# Revit family: LRTF
name_source: partatom
category: Lighting Fixtures
units: mm (PartAtom-declared; Revit-internal decimal feet)

## family parameters
Cut with Voids When Loaded = No
Host = Face
Light Source = Yes
Part Type = Normal
Room Calculation Point = No
Round Connector Dimension = Use Diameter
Shared = No

## types (8) — shared parameters
Assembly Code = D5020200
Color Filter = 16777215
Default Elevation = 4' - 0"
Description = LED Troffer Dish Low Profile Diffuser
Dimming Lamp Color Temperature Shift = <None>
Emit Shape Visible in Rendering = No
Housing Finish = Metal - Viscor - White
Lamp = LED
Lens Finish = Acrylic - Viscor - Frosted Ribbed Linear
Manufacturer = VISIONEERING by VISCOR
Model = LRTF
Tilt Angle = -90.00°
URL = https://www.viscor.com
Voltage = 120 V

## per-type parameters (varying)
| type | Apparent Load | Emit from Rectangle Length | Emit from Rectangle Width | Height of Fixture | Lamp Wattage | Length | Photometric Web File | Reflector Wdith | Width |
| LRTF1X4-LED840K050LUNV | 37 VA | 3' - 11 3/4" | 0' - 11 3/4" | 0' - 2 1/2" | 37 VA | 3' - 11 3/4" | LRTF1X4-LED840K050LUNV-G001831.IES | 0' - 5 7/8" | 0' - 11 3/4" |
| LRTF1x1-LED840K016LUNV | 17 VA | 1' - 1 15/16" | 1' - 1 15/16" | 0' - 3 3/8" | 17 VA | 1' - 1 15/16" | LRTF1x1-LED840K016LUNV.ies | 0' - 6 31/32" | 1' - 1 15/16" |
| LRTF2x2-LED840K038LUNV | 30 VA | 1' - 11 3/4" | 1' - 11 3/4" | 0' - 2 1/2" | 30 VA | 1' - 11 3/4" | LRTF2x2-LED840K038LUNV-G001332.IES | 0' - 11 7/8" | 1' - 11 3/4" |
| LRTF2X4-LED840K040LUNV | 32 VA | 3' - 11 3/4" | 1' - 11 3/4" | 0' - 2 1/2" | 32 VA | 3' - 11 3/4" | LRTF2X4-LED840K040LUNV.ies | 0' - 11 7/8" | 1' - 11 3/4" |
| LRTF30x30-LED840K038LUNV | 31 VA | 2' - 5 3/4" | 2' - 5 3/4" | 0' - 2 1/2" | 31 VA | 2' - 5 3/4" | LRTF30X30-LED840K038LUNV.ies | 1' - 2 7/8" | 2' - 5 3/4" |
| LRTF20x60-LED835K050LUNV | 37 VA | 4' - 11 3/4" | 1' - 7 3/4" | 0' - 2 1/2" | 37 VA | 4' - 11 3/4" | LRTF20X60-LED835K050LUNV.ies | 0' - 9 7/8" | 1' - 7 3/4" |
| LRTF2X4-LED840K050LUNV | 37 VA | 3' - 11 3/4" | 1' - 11 3/4" | 0' - 2 1/2" | 37 VA | 3' - 11 3/4" | LRTF2X4-LED840K050LUNV-G001504.IES | 0' - 11 7/8" | 1' - 11 3/4" |
| LRTF2X4-LED840K070LUNV | 55 VA | 3' - 11 3/4" | 1' - 11 3/4" | 0' - 2 1/2" | 55 VA | 3' - 11 3/4" | LRTF2X4-LED840K070LUNV-G001509.IES | 0' - 11 7/8" | 1' - 11 3/4" |

## geometry (parser evidence)
native form markers: Sweep x4
no freeform markers — native parametric forms only
